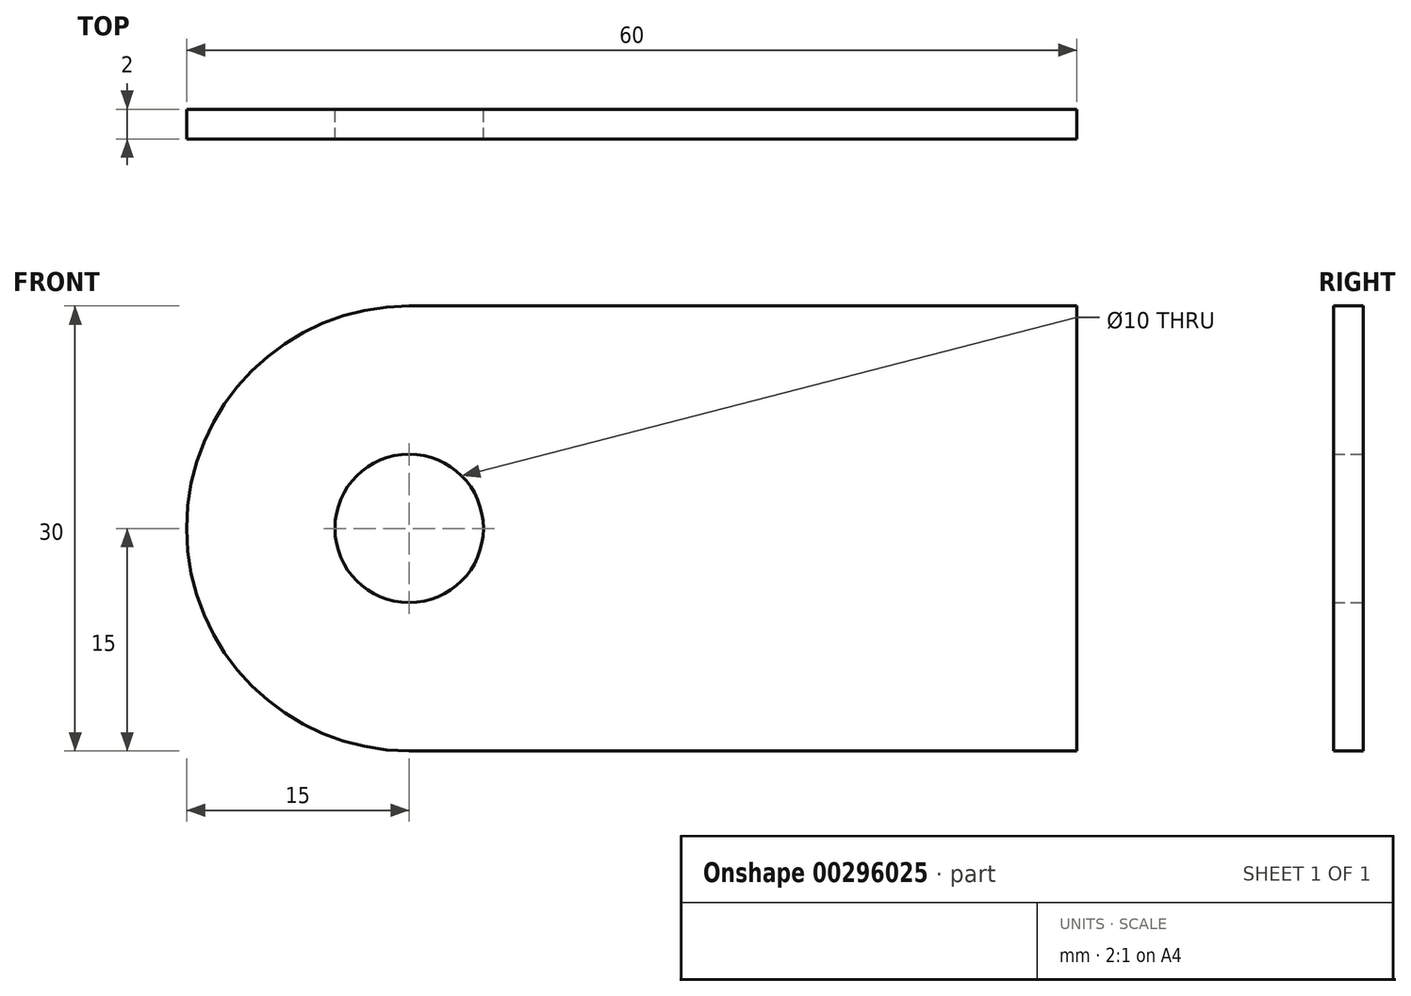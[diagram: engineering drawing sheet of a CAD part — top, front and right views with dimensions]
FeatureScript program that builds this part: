
annotation { "Feature Type Name" : "Feature", "Feature Type Description" : "" }
export const myFeature = defineFeature(function(context is Context, id is Id, definition is map)
    precondition{}
    {
        {
            var Q0;
            Q0=qCreatedBy(makeId("Front.planeOp"),FACE);
            var sketch = newSketch(context, id + "F0", { "sketchPlane" : qUnion([Q0])});
            skLineSegment(sketch, "E0.bottom", {"start": v(0, 0) * mm, "end": v(-45, 0) * mm});
            skLineSegment(sketch, "E0.top", {"start": v(0, -30) * mm, "end": v(-45, -30) * mm});
            skLineSegment(sketch, "E0.left", {"start": v(0, 0) * mm, "end": v(0, -30) * mm});
            skLineSegment(sketch, "E0.right", {"start": v(-60, -15) * mm, "end": v(-60, -15) * mm});
            skPoint(sketch, "E1.visualSharp", {"position": v(-60, 0) * mm});
            skArc(sketch, "E1.filletArc", {"start": v(-45, 0) * mm, "mid": v(-55.6, -4.4) * mm, "end": v(-60, -15) * mm});
            skPoint(sketch, "E2.visualSharp", {"position": v(-60, -30) * mm});
            skArc(sketch, "E2.filletArc", {"start": v(-60, -15) * mm, "mid": v(-55.6, -25.6) * mm, "end": v(-45, -30) * mm});
            skCircle(sketch, "E3", {"center": v(-45, -15) * mm, "radius": 5 * mm});
            skSolve(sketch);
        }
        {
            var Q0;
            Q0 = qSketchRegion(id + "F0", true);
            extrude(context, id + "F1", {"entities" : qUnion([Q0]), "depth" : 2 * mm});
        }
    });
